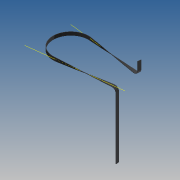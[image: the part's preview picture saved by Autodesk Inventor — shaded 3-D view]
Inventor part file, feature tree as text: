
AUTODESK INVENTOR PART (.ipt)
format: ipt  version: 2013 (Build 170138000, 138)  size: 164,864 bytes
history: native  units: mm
features: sketch x8, extrude x4, other x2, helix x2, revolve x2, reference x2
ambient origin geometry x8: Origin, YZ Plane, XZ Plane, XY Plane, X Axis, Y Axis, Z Axis, Center Point
bodies: Solid1 (feature_tree)
feature tree (20):
  extrude  "Extrusion1"  Depth=0.254mm
  extrude  "Extrusion2"  Depth=6.0mm TaperAngle=0.0deg
  sketch  "Sketch3"  dims[d9=0.254mm]
  other  "Work Axis1"
  helix  "Coil1"  [1 undecoded]
  sketch  "Sketch4"  dims[d10=91.864mm d11=92.864mm d12=2.5mm d13=0.0mm d14=90.0deg d15=90.0deg d16=0.0mm d17=0.0mm d18=0.254mm]
  other  "Work Axis2"
  helix  "Coil2"  [1 undecoded]
  revolve  "Revolution1"  [1 undecoded]
  revolve  "Revolution2"  [1 undecoded]
  extrude  "Extrusion5"  Depth=7.0mm
  extrude  "Extrusion4"  Depth=10.0mm TaperAngle=0.0deg
  sketch  "Sketch1"  dims[d0=63.661977mm d2=0.254mm]
  sketch  "Sketch2"  dims[d3=0.375mm d4=6.0mm d5=0.0mm d6=29.040533mm d7=0.0mm d8=0.0mm]
  sketch  "Sketch5"  dims[d19=91.864mm d20=92.864mm d21=2.5mm d22=0.0mm d23=90.0deg d24=90.0deg d25=0.0mm d26=0.0mm d27=7.0mm]
  sketch  "Sketch6"  dims[d28=90.0deg d29=7.0mm]
  sketch  "Sketch8"  dims[d30=90.0deg d34=10.0mm d35=0.0mm]
  reference  "Reference1"
  sketch  "Sketch9"  dims[d36=10.0mm d37=0.0mm]
  reference  "Reference2"
note: 4 required parameter values undecoded (feature->parameter linkage not recoverable at this tier; creation-order binding heuristic only, values carry confidence <= 0.55)